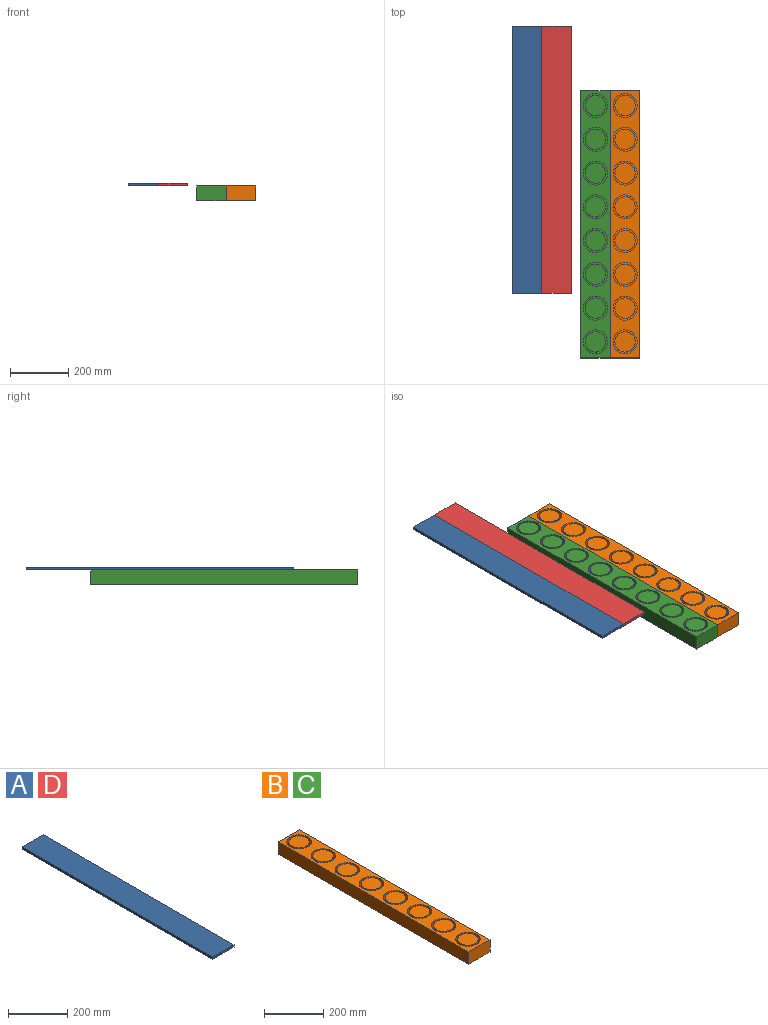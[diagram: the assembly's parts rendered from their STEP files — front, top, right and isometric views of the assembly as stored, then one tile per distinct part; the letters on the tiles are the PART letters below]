
ASSEMBLY  parts=4 mates=3
PART A: 6 faces, bbox 101.6x914.4x9.5 mm
  f0: plane 101.6x9.53mm, normal (0,1,0), area 967.7mm2, adj f1,f3,f4,f5
  f1: plane 914.4x9.53mm, normal (-1,0,0), area 8709.7mm2, adj f0,f2,f4,f5
  f2: plane 101.6x9.53mm, normal (0,-1,0), area 967.7mm2, adj f1,f3,f4,f5
  f3: plane 914.4x9.53mm, normal (1,0,0), area 8709.7mm2, adj f0,f2,f4,f5
  f4: plane 914.4x101.6mm, normal (0,0,1), area 92903mm2, adj f0,f1,f2,f3
  f5: plane 914.4x101.6mm, normal (0,0,-1), area 92903mm2, adj f0,f1,f2,f3
PART B: 38 faces, bbox 101.6x914.4x50.8 mm
  f0: cylinder r=34.92mm len=69.85mm, axis (0,0,1), area 11036.1mm2, adj f36,f37
  f1: cylinder r=34.92mm len=69.85mm, axis (0,0,1), area 11036.1mm2, adj f33,f34
  f2: cylinder r=34.92mm len=69.85mm, axis (0,0,1), area 11036.1mm2, adj f30,f31
  f3: cylinder r=34.92mm len=69.85mm, axis (0,0,1), area 11036.1mm2, adj f27,f28
  f4: cylinder r=34.92mm len=69.85mm, axis (0,0,1), area 11036.1mm2, adj f24,f25
  f5: cylinder r=34.92mm len=69.85mm, axis (0,0,1), area 11036.1mm2, adj f21,f22
  f6: cylinder r=34.92mm len=69.85mm, axis (0,0,1), area 11036.1mm2, adj f18,f19
  f7: cylinder r=34.92mm len=69.85mm, axis (0,0,1), area 11036.1mm2, adj f15,f16
  f8: plane 101.6x50.8mm, normal (0,1,0), area 5161.3mm2, adj f9,f11,f12,f13
  f9: plane 914.4x50.8mm, normal (-1,0,0), area 46451.5mm2, adj f8,f10,f12,f13
  f10: plane 101.6x50.8mm, normal (0,-1,0), area 5161.3mm2, adj f9,f11,f12,f13
  f11: plane 914.4x50.8mm, normal (1,0,0), area 46451.5mm2, adj f8,f10,f12,f13
  f12: plane 914.4x101.6mm, normal (0,0,1), area 50086.3mm2, adj f8,f9,f10,f11,f14,f17,f20,f23
  f13: plane 914.4x101.6mm, normal (0,0,-1), area 92903mm2, adj f8,f9,f10,f11
  f14: cylinder r=41.27mm len=82.55mm, axis (0,0,1), area 13108.5mm2, adj f12,f15
  f15: plane 82.55x82.55mm, normal (0,0,1), area 1520.1mm2, adj f7,f14
  f16: plane 69.85x69.85mm, normal (0,0,1), area 3832mm2, adj f7
  f17: cylinder r=41.27mm len=82.55mm, axis (0,0,1), area 13108.5mm2, adj f12,f18
  f18: plane 82.55x82.55mm, normal (0,0,1), area 1520.1mm2, adj f6,f17
  f19: plane 69.85x69.85mm, normal (0,0,1), area 3832mm2, adj f6
  f20: cylinder r=41.27mm len=82.55mm, axis (0,0,1), area 13108.5mm2, adj f12,f21
  f21: plane 82.55x82.55mm, normal (0,0,1), area 1520.1mm2, adj f5,f20
  f22: plane 69.85x69.85mm, normal (0,0,1), area 3832mm2, adj f5
  f23: cylinder r=41.27mm len=82.55mm, axis (0,0,1), area 13108.5mm2, adj f12,f24
  f24: plane 82.55x82.55mm, normal (0,0,1), area 1520.1mm2, adj f4,f23
  f25: plane 69.85x69.85mm, normal (0,0,1), area 3832mm2, adj f4
  f26: cylinder r=41.27mm len=82.55mm, axis (0,0,1), area 13108.5mm2, adj f12,f27
  f27: plane 82.55x82.55mm, normal (0,0,1), area 1520.1mm2, adj f3,f26
  f28: plane 69.85x69.85mm, normal (0,0,1), area 3832mm2, adj f3
  f29: cylinder r=41.27mm len=82.55mm, axis (0,0,1), area 13108.5mm2, adj f12,f30
  f30: plane 82.55x82.55mm, normal (0,0,1), area 1520.1mm2, adj f2,f29
  f31: plane 69.85x69.85mm, normal (0,0,1), area 3832mm2, adj f2
  f32: cylinder r=41.27mm len=82.55mm, axis (0,0,1), area 13108.5mm2, adj f12,f33
  f33: plane 82.55x82.55mm, normal (0,0,1), area 1520.1mm2, adj f1,f32
  f34: plane 69.85x69.85mm, normal (0,0,1), area 3832mm2, adj f1
  f35: cylinder r=41.27mm len=82.55mm, axis (0,0,1), area 13108.5mm2, adj f12,f36
  f36: plane 82.55x82.55mm, normal (0,0,1), area 1520.1mm2, adj f0,f35
  f37: plane 69.85x69.85mm, normal (0,0,1), area 3832mm2, adj f0
PART C: same geometry as B
PART D: same geometry as A
PLACE A t=(-765.96,462.32,93)mm
PLACE B t=(-429.86,239.98,42.2)mm
PLACE C t=(-531.46,239.98,42.2)mm
PLACE D t=(-664.36,462.32,93)mm
MATE fastened C.f11 <-> B.f9  axis (1,0,0) through (-429.86,-217.22,67.6)mm
MATE fastened D.f1 <-> A.f3  axis (-1,0,0) through (-664.36,5.12,97.76)mm
MATE planar B.f12 <-> D.f5  axis (0,0,1) through (-379.06,-219.4,93)mm
